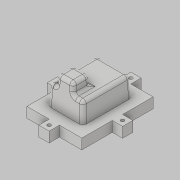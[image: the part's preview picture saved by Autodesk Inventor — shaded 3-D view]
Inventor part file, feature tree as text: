
AUTODESK INVENTOR PART (.ipt)
format: ipt  version: 2019 (Build 230136000, 136)  size: 343,040 bytes
history: native  units: mm
features: fillet x5, extrude x4, other x3, sketch x3, shell x1, plane x1, boolean_combine x1, delete_face x1
ambient origin geometry x8: Origin, YZ Plane, XZ Plane, XY Plane, X Axis, Y Axis, Z Axis, Center Point
bodies: Solid2 (feature_tree)
feature tree (19):
  other  "Sólido1"
  sketch  "Boceto1"  dims[d0=50.0mm d1=30.0mm]
  extrude  "Extrusión1"  Depth=30.0mm
  extrude  "Extrusión2"  Depth=10.0mm
  other  "Cara para el ángulo de desmoldeo2"
  other  "Cara para el ángulo de desmoldeo3"
  fillet  "Empalme1"  Radius=25.0mm
  fillet  "Empalme2"  Radius=70.0mm
  fillet  "Empalme3"  Radius=25.0mm
  fillet  "Empalme4"  Radius=3.0mm
  fillet  "Empalme5"  Radius=6.0mm
  shell  "Vaciado1"  Thickness=6.0mm
  plane  "Work Plane1"
  extrude  "Extrusion3"  Depth=15.0mm
  boolean_combine  "Combine1"
  delete_face  "Delete Face1"
  extrude  "Extrusion6"  Depth=6.0mm
  sketch  "Sketch2"  dims[d2=10.0mm d3=10.0mm d4=25.0mm d5=70.0mm d6=0.0mm d7=25.0mm d8=0.0mm d9=3.0mm d10=6.0mm d11=6.0mm]
  sketch  "Sketch3"  dims[d12=3.0mm d13=1.0mm d15=6.0mm d16=0.523599mm d17=0.523599mm d18=15.0mm d19=15.0mm d21=180.0deg d23=0.0mm d24=80.0mm d25=0.0mm d26=15.0mm d27=30.0mm d28=30.0mm d29=15.0mm d30=15.0mm d31=30.0mm d32=30.0mm d33=5.0mm d34=7.5mm d35=5.0mm d36=7.5mm d37=5.0mm d38=7.5mm d39=5.0mm d40=7.5mm d49=15.0mm d50=0.0mm]
